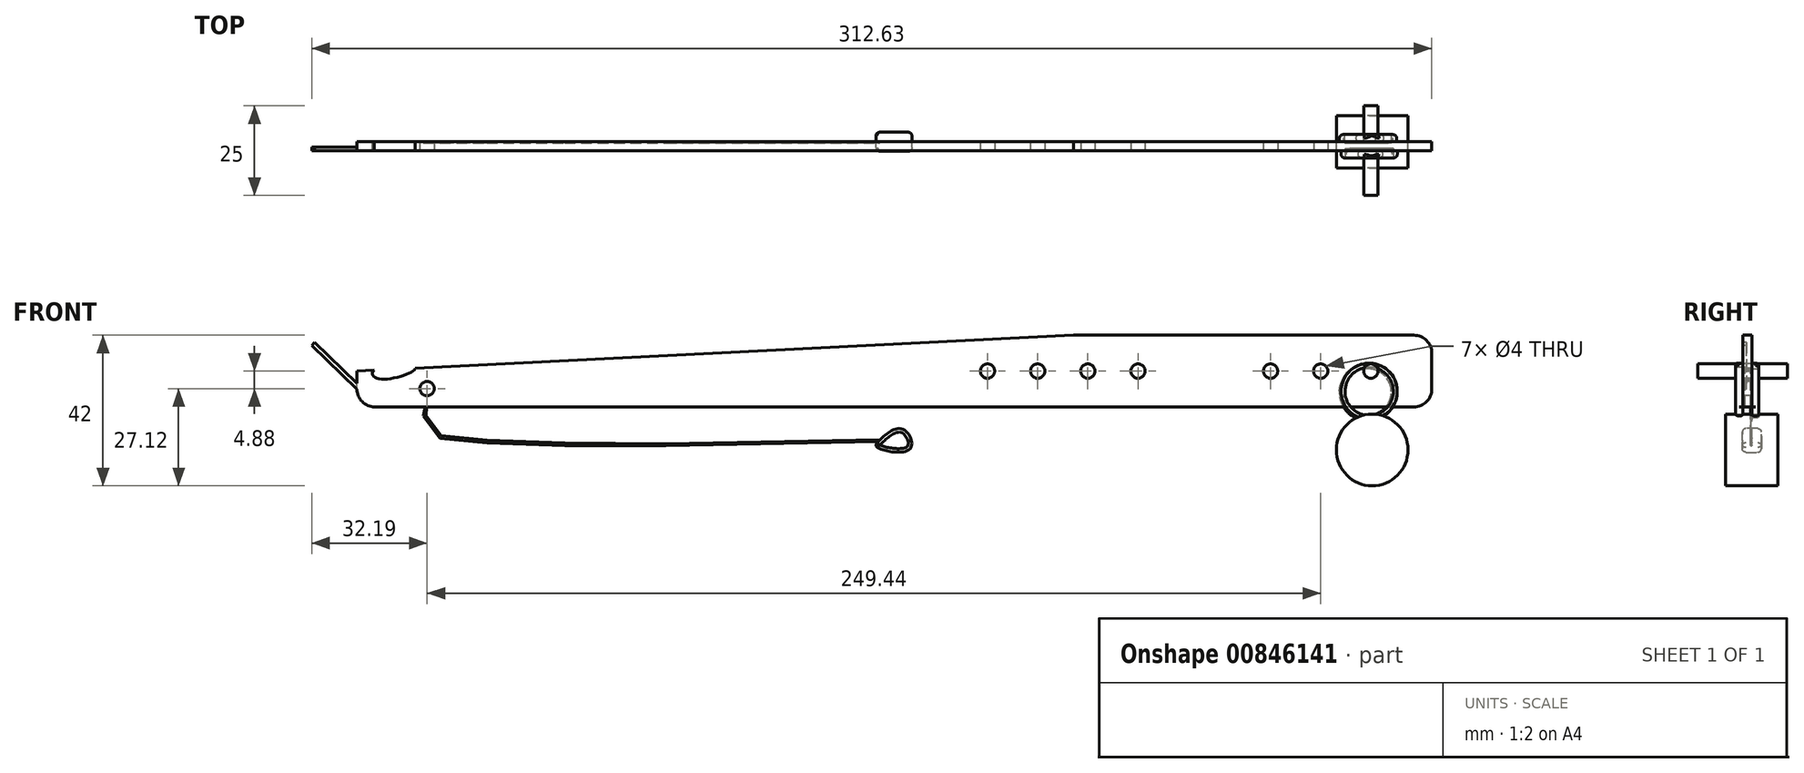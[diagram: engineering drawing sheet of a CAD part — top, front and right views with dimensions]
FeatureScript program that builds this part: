
annotation { "Feature Type Name" : "Feature", "Feature Type Description" : "" }
export const myFeature = defineFeature(function(context is Context, id is Id, definition is map)
    precondition{}
    {
        {
            var Q0;
            Q0=qCreatedBy(makeId("Front.planeOp"),FACE);
            var sketch = newSketch(context, id + "F0", { "sketchPlane" : qUnion([Q0])});
            skLineSegment(sketch, "E0.bottom", {"start": v(150, -10) * mm, "end": v(-150, -10) * mm});
            skLineSegment(sketch, "E0.top", {"start": v(150, 10) * mm, "end": v(-150, 10) * mm});
            skLineSegment(sketch, "E0.left", {"start": v(150, -10) * mm, "end": v(150, 10) * mm});
            skLineSegment(sketch, "E0.right", {"start": v(-150, -10) * mm, "end": v(-150, 10) * mm});
            skPoint(sketch, "E0.middle", {"position": v(0, 0) * mm});
            skSolve(sketch);
        }
        {
            var Q0;
            Q0 = qSketchRegion(id + "F0", true);
            extrude(context, id + "F1", {"entities" : qUnion([Q0]), "depth" : 2.5 * mm, "offsetDistance" : 25 * mm});
        }
        {
            var Q0;
            Q0=makeQuery(id+"F1.opExtrude","SWEPT_EDGE",EDGE,{"disambiguationData":[OSD([sQuery(id+"F0.wireOp",EDGE,"E0.top"),sQuery(id+"F0.wireOp",EDGE,"E0.right")])]});
            chamfer(context, id + "F2", {"entities" : qUnion([Q0]), "chamferType" : ChamferType.TWO_OFFSETS, "width1" : 10 * mm, "oppositeDirection" : false, "width2" : 200 * mm, "tangentPropagation" : true});
        }
        {
            var Q0;
            Q0=makeQuery(id+"F1.opExtrude","SWEPT_EDGE",EDGE,{"disambiguationData":[OSD([sQuery(id+"F0.wireOp",EDGE,"E0.bottom"),sQuery(id+"F0.wireOp",EDGE,"E0.right")])]});
            fillet(context, id + "F3", {"entities" : qUnion([Q0]), "radius" : 5 * mm, "tangentPropagation" : true, "allowEdgeOverflow" : false});
        }
        {
            var Q0;
            Q0=makeQuery(id+"F1.opExtrude","SWEPT_EDGE",EDGE,{"disambiguationData":[OSD([sQuery(id+"F0.wireOp",EDGE,"E0.top"),sQuery(id+"F0.wireOp",EDGE,"E0.left")])]});
            fillet(context, id + "F4", {"entities" : qUnion([Q0]), "radius" : 5 * mm, "tangentPropagation" : true, "allowEdgeOverflow" : false});
        }
        {
            var Q0;
            Q0=makeQuery(id+"F1.opExtrude","SWEPT_EDGE",EDGE,{"disambiguationData":[OSD([sQuery(id+"F0.wireOp",EDGE,"E0.bottom"),sQuery(id+"F0.wireOp",EDGE,"E0.left")])]});
            fillet(context, id + "F5", {"entities" : qUnion([Q0]), "radius" : 5 * mm, "tangentPropagation" : true, "allowEdgeOverflow" : false});
        }
        {
            var Q0;
            Q0=makeQuery(id+"F1.opExtrude","CAP_FACE",FACE,{"disambiguationData":[OSD([sQuery(id+"F0.wireOp",EDGE,"E0.bottom"),sQuery(id+"F0.wireOp",EDGE,"E0.top"),sQuery(id+"F0.wireOp",EDGE,"E0.left"),sQuery(id+"F0.wireOp",EDGE,"E0.right")])],"isStart":false});
            var sketch = newSketch(context, id + "F6", { "sketchPlane" : qUnion([Q0])});
            skFitSpline(sketch, "E1", {"points": [v(-145.2, 0.24) * mm, v(-144.14, -2.13) * mm, v(-133.8, 0.8) * mm, v(-145.2, 0.24) * mm]});
            skSolve(sketch);
        }
        {
            var Q0;
            Q0 = qSketchRegion(id + "F6", true);
            extrude(context, id + "F7", {"entities" : qUnion([Q0]), "operationType" : NewBodyOperationType.REMOVE, "oppositeDirection" : true, "depth" : 6 * mm, "offsetDistance" : 25 * mm});
        }
        {
            var Q0;
            Q0=makeQuery(id+"F1.opExtrude","CAP_FACE",FACE,{"disambiguationData":[OSD([sQuery(id+"F0.wireOp",EDGE,"E0.bottom"),sQuery(id+"F0.wireOp",EDGE,"E0.top"),sQuery(id+"F0.wireOp",EDGE,"E0.left"),sQuery(id+"F0.wireOp",EDGE,"E0.right")])],"isStart":false});
            var sketch = newSketch(context, id + "F8", { "sketchPlane" : qUnion([Q0])});
            skLineSegment(sketch, "E2", {"start": v(-150, -5) * mm, "end": v(-162.63, 7.1) * mm});
            skLineSegment(sketch, "E3", {"start": v(-162.63, 7.1) * mm, "end": v(-161.82, 7.96) * mm});
            skLineSegment(sketch, "E4", {"start": v(-161.82, 7.96) * mm, "end": v(-150, -3.37) * mm});
            skLineSegment(sketch, "E5", {"start": v(-150, -3.37) * mm, "end": v(-150, -5) * mm});
            skSolve(sketch);
        }
        {
            var Q0;
            Q0 = qSketchRegion(id + "F8", true);
            extrude(context, id + "F9", {"entities" : qUnion([Q0]), "operationType" : NewBodyOperationType.ADD, "oppositeDirection" : true, "depth" : 1 * mm, "offsetDistance" : 25 * mm});
        }
        {
            var Q0;
            Q0=makeQuery(id+"F9.boolean.opBoolean","MERGE",FACE,{"derivedFrom":[makeQuery(id+"F1.opExtrude","CAP_FACE",FACE,{"disambiguationData":[OSD([sQuery(id+"F0.wireOp",EDGE,"E0.bottom"),sQuery(id+"F0.wireOp",EDGE,"E0.top"),sQuery(id+"F0.wireOp",EDGE,"E0.left"),sQuery(id+"F0.wireOp",EDGE,"E0.right")])],"isStart":false}),makeQuery(id+"F9.opExtrude","CAP_FACE",FACE,{"disambiguationData":[OSD([sQuery(id+"F8.wireOp",EDGE,"E2"),sQuery(id+"F8.wireOp",EDGE,"E3"),sQuery(id+"F8.wireOp",EDGE,"E4"),sQuery(id+"F8.wireOp",EDGE,"E5")])],"isStart":true})]});
            var sketch = newSketch(context, id + "F10", { "sketchPlane" : qUnion([Q0])});
            skCircle(sketch, "E6", {"center": v(-130.44, -4.88) * mm, "radius": 2 * mm});
            skSolve(sketch);
        }
        {
            var Q0;
            Q0 = qSketchRegion(id + "F10", true);
            extrude(context, id + "F11", {"entities" : qUnion([Q0]), "operationType" : NewBodyOperationType.REMOVE, "oppositeDirection" : true, "depth" : 25 * mm, "offsetDistance" : 25 * mm});
        }
        {
            var Q0;
            Q0=makeQuery(id+"F9.boolean.opBoolean","MERGE",FACE,{"derivedFrom":[makeQuery(id+"F1.opExtrude","CAP_FACE",FACE,{"disambiguationData":[OSD([sQuery(id+"F0.wireOp",EDGE,"E0.bottom"),sQuery(id+"F0.wireOp",EDGE,"E0.top"),sQuery(id+"F0.wireOp",EDGE,"E0.left"),sQuery(id+"F0.wireOp",EDGE,"E0.right")])],"isStart":false}),makeQuery(id+"F9.opExtrude","CAP_FACE",FACE,{"disambiguationData":[OSD([sQuery(id+"F8.wireOp",EDGE,"E2"),sQuery(id+"F8.wireOp",EDGE,"E3"),sQuery(id+"F8.wireOp",EDGE,"E4"),sQuery(id+"F8.wireOp",EDGE,"E5")])],"isStart":true})]});
            var sketch = newSketch(context, id + "F12", { "sketchPlane" : qUnion([Q0])});
            skCircle(sketch, "E7", {"center": v(133, 0) * mm, "radius": 2 * mm});
            skSolve(sketch);
        }
        {
            var Q0;
            Q0 = qSketchRegion(id + "F12", true);
            extrude(context, id + "F13", {"entities" : qUnion([Q0]), "operationType" : NewBodyOperationType.ADD, "endBound" : BoundingType.SYMMETRIC, "oppositeDirection" : true, "depth" : 25 * mm, "offsetDistance" : 25 * mm});
        }
        {
            var Q0;
            Q0=makeQuery(id+"F9.boolean.opBoolean","MERGE",FACE,{"derivedFrom":[makeQuery(id+"F1.opExtrude","CAP_FACE",FACE,{"disambiguationData":[OSD([sQuery(id+"F0.wireOp",EDGE,"E0.bottom"),sQuery(id+"F0.wireOp",EDGE,"E0.top"),sQuery(id+"F0.wireOp",EDGE,"E0.left"),sQuery(id+"F0.wireOp",EDGE,"E0.right")])],"isStart":false}),makeQuery(id+"F9.opExtrude","CAP_FACE",FACE,{"disambiguationData":[OSD([sQuery(id+"F8.wireOp",EDGE,"E2"),sQuery(id+"F8.wireOp",EDGE,"E3"),sQuery(id+"F8.wireOp",EDGE,"E4"),sQuery(id+"F8.wireOp",EDGE,"E5")])],"isStart":true})]});
            var sketch = newSketch(context, id + "F14", { "sketchPlane" : qUnion([Q0])});
            skCircle(sketch, "E8", {"center": v(119, 0) * mm, "radius": 2 * mm});
            skSolve(sketch);
        }
        {
            var Q0;
            Q0=makeQuery(id+"F14.imprint","IMPRINT",FACE,{"disambiguationData":[TD([[makeQuery(id+"F14.imprint","IMPRINT",EDGE,{"derivedFrom":sQuery(id+"F14.wireOp",EDGE,"E8")}),-1.0]])]});
            var sketch = newSketch(context, id + "F15", { "sketchPlane" : qUnion([Q0])});
            skCircle(sketch, "E9", {"center": v(105, 0) * mm, "radius": 2 * mm});
            skSolve(sketch);
        }
        {
            var Q0;
            Q0 = qSketchRegion(id + "F14", true);
            extrude(context, id + "F16", {"entities" : qUnion([Q0]), "operationType" : NewBodyOperationType.REMOVE, "oppositeDirection" : true, "depth" : 25 * mm, "offsetDistance" : 25 * mm});
        }
        {
            var Q0;
            Q0 = qSketchRegion(id + "F15", true);
            extrude(context, id + "F17", {"entities" : qUnion([Q0]), "operationType" : NewBodyOperationType.REMOVE, "oppositeDirection" : true, "depth" : 25 * mm, "offsetDistance" : 25 * mm});
        }
        {
            var Q0;
            Q0=makeQuery(id+"F9.boolean.opBoolean","MERGE",FACE,{"derivedFrom":[makeQuery(id+"F1.opExtrude","CAP_FACE",FACE,{"disambiguationData":[OSD([sQuery(id+"F0.wireOp",EDGE,"E0.bottom"),sQuery(id+"F0.wireOp",EDGE,"E0.top"),sQuery(id+"F0.wireOp",EDGE,"E0.left"),sQuery(id+"F0.wireOp",EDGE,"E0.right")])],"isStart":false}),makeQuery(id+"F9.opExtrude","CAP_FACE",FACE,{"disambiguationData":[OSD([sQuery(id+"F8.wireOp",EDGE,"E2"),sQuery(id+"F8.wireOp",EDGE,"E3"),sQuery(id+"F8.wireOp",EDGE,"E4"),sQuery(id+"F8.wireOp",EDGE,"E5")])],"isStart":true})]});
            var sketch = newSketch(context, id + "F18", { "sketchPlane" : qUnion([Q0])});
            skCircle(sketch, "E10", {"center": v(68, 0) * mm, "radius": 2 * mm});
            skSolve(sketch);
        }
        {
            var Q0;
            Q0 = qSketchRegion(id + "F18", true);
            extrude(context, id + "F19", {"entities" : qUnion([Q0]), "operationType" : NewBodyOperationType.REMOVE, "oppositeDirection" : true, "depth" : 25 * mm, "offsetDistance" : 25 * mm});
        }
        {
            var Q0;
            Q0=makeQuery(id+"F9.boolean.opBoolean","MERGE",FACE,{"derivedFrom":[makeQuery(id+"F1.opExtrude","CAP_FACE",FACE,{"disambiguationData":[OSD([sQuery(id+"F0.wireOp",EDGE,"E0.bottom"),sQuery(id+"F0.wireOp",EDGE,"E0.top"),sQuery(id+"F0.wireOp",EDGE,"E0.left"),sQuery(id+"F0.wireOp",EDGE,"E0.right")])],"isStart":false}),makeQuery(id+"F9.opExtrude","CAP_FACE",FACE,{"disambiguationData":[OSD([sQuery(id+"F8.wireOp",EDGE,"E2"),sQuery(id+"F8.wireOp",EDGE,"E3"),sQuery(id+"F8.wireOp",EDGE,"E4"),sQuery(id+"F8.wireOp",EDGE,"E5")])],"isStart":true})]});
            var sketch = newSketch(context, id + "F20", { "sketchPlane" : qUnion([Q0])});
            skCircle(sketch, "E11", {"center": v(54, 0) * mm, "radius": 2 * mm});
            skSolve(sketch);
        }
        {
            var Q0;
            Q0 = qSketchRegion(id + "F20", true);
            extrude(context, id + "F21", {"entities" : qUnion([Q0]), "operationType" : NewBodyOperationType.REMOVE, "oppositeDirection" : true, "depth" : 25 * mm, "offsetDistance" : 25 * mm});
        }
        {
            var Q0;
            Q0=makeQuery(id+"F9.boolean.opBoolean","MERGE",FACE,{"derivedFrom":[makeQuery(id+"F1.opExtrude","CAP_FACE",FACE,{"disambiguationData":[OSD([sQuery(id+"F0.wireOp",EDGE,"E0.bottom"),sQuery(id+"F0.wireOp",EDGE,"E0.top"),sQuery(id+"F0.wireOp",EDGE,"E0.left"),sQuery(id+"F0.wireOp",EDGE,"E0.right")])],"isStart":false}),makeQuery(id+"F9.opExtrude","CAP_FACE",FACE,{"disambiguationData":[OSD([sQuery(id+"F8.wireOp",EDGE,"E2"),sQuery(id+"F8.wireOp",EDGE,"E3"),sQuery(id+"F8.wireOp",EDGE,"E4"),sQuery(id+"F8.wireOp",EDGE,"E5")])],"isStart":true})]});
            var sketch = newSketch(context, id + "F22", { "sketchPlane" : qUnion([Q0])});
            skCircle(sketch, "E12", {"center": v(40, 0) * mm, "radius": 2 * mm});
            skSolve(sketch);
        }
        {
            var Q0;
            Q0 = qSketchRegion(id + "F22", true);
            extrude(context, id + "F23", {"entities" : qUnion([Q0]), "operationType" : NewBodyOperationType.REMOVE, "oppositeDirection" : true, "depth" : 25 * mm, "offsetDistance" : 25 * mm});
        }
        {
            var Q0;
            Q0=makeQuery(id+"F9.boolean.opBoolean","MERGE",FACE,{"derivedFrom":[makeQuery(id+"F1.opExtrude","CAP_FACE",FACE,{"disambiguationData":[OSD([sQuery(id+"F0.wireOp",EDGE,"E0.bottom"),sQuery(id+"F0.wireOp",EDGE,"E0.top"),sQuery(id+"F0.wireOp",EDGE,"E0.left"),sQuery(id+"F0.wireOp",EDGE,"E0.right")])],"isStart":false}),makeQuery(id+"F9.opExtrude","CAP_FACE",FACE,{"disambiguationData":[OSD([sQuery(id+"F8.wireOp",EDGE,"E2"),sQuery(id+"F8.wireOp",EDGE,"E3"),sQuery(id+"F8.wireOp",EDGE,"E4"),sQuery(id+"F8.wireOp",EDGE,"E5")])],"isStart":true})]});
            var sketch = newSketch(context, id + "F24", { "sketchPlane" : qUnion([Q0])});
            skCircle(sketch, "E13", {"center": v(26, 0) * mm, "radius": 2 * mm});
            skSolve(sketch);
        }
        {
            var Q0;
            Q0 = qSketchRegion(id + "F24", true);
            extrude(context, id + "F25", {"entities" : qUnion([Q0]), "operationType" : NewBodyOperationType.REMOVE, "oppositeDirection" : true, "depth" : 25 * mm, "offsetDistance" : 25 * mm});
        }
        {
            var Q0;
            Q0=makeQuery(id+"F9.boolean.opBoolean","MERGE",FACE,{"derivedFrom":[makeQuery(id+"F1.opExtrude","CAP_FACE",FACE,{"disambiguationData":[OSD([sQuery(id+"F0.wireOp",EDGE,"E0.bottom"),sQuery(id+"F0.wireOp",EDGE,"E0.top"),sQuery(id+"F0.wireOp",EDGE,"E0.left"),sQuery(id+"F0.wireOp",EDGE,"E0.right")])],"isStart":false}),makeQuery(id+"F9.opExtrude","CAP_FACE",FACE,{"disambiguationData":[OSD([sQuery(id+"F8.wireOp",EDGE,"E2"),sQuery(id+"F8.wireOp",EDGE,"E3"),sQuery(id+"F8.wireOp",EDGE,"E4"),sQuery(id+"F8.wireOp",EDGE,"E5")])],"isStart":true})]});
            var sketch = newSketch(context, id + "F26", { "sketchPlane" : qUnion([Q0])});
            skCircle(sketch, "E14", {"center": v(132.53, -5.65) * mm, "radius": 7.84 * mm});
            skSolve(sketch);
        }
        {
            var Q0;
            Q0 = qSketchRegion(id + "F26", true);
            extrude(context, id + "F27", {"entities" : qUnion([Q0]), "operationType" : NewBodyOperationType.ADD, "depth" : 2 * mm, "offsetDistance" : 25 * mm});
        }
        {
            var Q0;
            Q0=makeQuery(id+"F27.opExtrude","CAP_FACE",FACE,{"disambiguationData":[OSD([sQuery(id+"F26.wireOp",EDGE,"E14")])],"isStart":false});
            var sketch = newSketch(context, id + "F28", { "sketchPlane" : qUnion([Q0])});
            skCircle(sketch, "E15", {"center": v(132.53, -5.65) * mm, "radius": 6.74 * mm});
            skSolve(sketch);
        }
        {
            var Q0;
            Q0 = qSketchRegion(id + "F28", true);
            extrude(context, id + "F29", {"entities" : qUnion([Q0]), "operationType" : NewBodyOperationType.REMOVE, "oppositeDirection" : true, "depth" : 2.6 * mm, "offsetDistance" : 25 * mm});
        }
        {
            var Q0;
            Q0=makeQuery(id+"F1.opExtrude","CAP_FACE",FACE,{"disambiguationData":[OSD([sQuery(id+"F0.wireOp",EDGE,"E0.bottom"),sQuery(id+"F0.wireOp",EDGE,"E0.top"),sQuery(id+"F0.wireOp",EDGE,"E0.left"),sQuery(id+"F0.wireOp",EDGE,"E0.right")])],"isStart":true});
            var sketch = newSketch(context, id + "F30", { "sketchPlane" : qUnion([Q0])});
            skCircle(sketch, "E16", {"center": v(-132.22, -5.88) * mm, "radius": 8 * mm});
            skSolve(sketch);
        }
        {
            var Q0;
            Q0 = qSketchRegion(id + "F30", true);
            extrude(context, id + "F31", {"entities" : qUnion([Q0]), "operationType" : NewBodyOperationType.ADD, "depth" : 2 * mm, "offsetDistance" : 25 * mm});
        }
        {
            var Q0;
            Q0=makeQuery(id+"F31.opExtrude","CAP_FACE",FACE,{"disambiguationData":[OSD([sQuery(id+"F30.wireOp",EDGE,"E16")])],"isStart":false});
            var sketch = newSketch(context, id + "F32", { "sketchPlane" : qUnion([Q0])});
            skCircle(sketch, "E17", {"center": v(-132.22, -5.88) * mm, "radius": 6.5 * mm});
            skSolve(sketch);
        }
        {
            var Q0;
            Q0 = qSketchRegion(id + "F32", true);
            extrude(context, id + "F33", {"entities" : qUnion([Q0]), "operationType" : NewBodyOperationType.REMOVE, "oppositeDirection" : true, "depth" : 2.4 * mm, "offsetDistance" : 25 * mm});
        }
        {
            var Q0;
            Q0=makeQuery(id+"F31.opExtrude","CAP_EDGE",EDGE,{"disambiguationData":[OSD([sQuery(id+"F30.wireOp",EDGE,"E16")])],"isStart":false});
            fillet(context, id + "F34", {"entities" : qUnion([Q0]), "radius" : 1 * mm, "tangentPropagation" : true, "allowEdgeOverflow" : false});
        }
        {
            var Q0;
            Q0=makeQuery(id+"F27.opExtrude","CAP_EDGE",EDGE,{"disambiguationData":[OSD([sQuery(id+"F26.wireOp",EDGE,"E14")])],"isStart":false});
            fillet(context, id + "F35", {"entities" : qUnion([Q0]), "radius" : 1 * mm, "tangentPropagation" : true, "allowEdgeOverflow" : false});
        }
        {
            var Q0;
            {var subQ0=sQuery(id+"F26.wireOp",EDGE,"E14");Q0=makeQuery(id+"F27.boolean.opBoolean","SPLIT",EDGE,{"disambiguationData":[topologyDisambiguationEdgeConnected([makeQuery(id+"F27.opExtrude","CAP_FACE",FACE,{"disambiguationData":[OSD([subQ0])],"isStart":true})])],"derivedFrom":makeQuery(id+"F27.opExtrude","CAP_EDGE",EDGE,{"disambiguationData":[OSD([subQ0])],"isStart":true})});}
            fillet(context, id + "F36", {"entities" : qUnion([Q0]), "radius" : 1 * mm, "tangentPropagation" : true, "allowEdgeOverflow" : false});
        }
        {
            var Q0;
            {var subQ0=sQuery(id+"F30.wireOp",EDGE,"E16");Q0=makeQuery(id+"F31.boolean.opBoolean","SPLIT",EDGE,{"disambiguationData":[topologyDisambiguationEdgeConnected([makeQuery(id+"F31.opExtrude","CAP_FACE",FACE,{"disambiguationData":[OSD([subQ0])],"isStart":true})])],"derivedFrom":makeQuery(id+"F31.opExtrude","CAP_EDGE",EDGE,{"disambiguationData":[OSD([subQ0])],"isStart":true})});}
            fillet(context, id + "F37", {"entities" : qUnion([Q0]), "radius" : 1 * mm, "tangentPropagation" : true, "allowEdgeOverflow" : false});
        }
        {
            var Q0;
            Q0=qCreatedBy(makeId("Front.planeOp"),FACE);
            var sketch = newSketch(context, id + "F38", { "sketchPlane" : qUnion([Q0])});
            skLineSegment(sketch, "E18", {"start": v(-130.5, -6.89) * mm, "end": v(-131.46, -12.56) * mm});
            skLineSegment(sketch, "E19", {"start": v(-131.46, -12.56) * mm, "end": v(-126.84, -18.75) * mm});
            skLineSegment(sketch, "E20", {"start": v(-126.84, -18.75) * mm, "end": v(-113.75, -20) * mm});
            skLineSegment(sketch, "E21", {"start": v(-113.75, -20) * mm, "end": v(-92.04, -20.75) * mm});
            skLineSegment(sketch, "E22", {"start": v(-92.04, -20.75) * mm, "end": v(-63.78, -20.75) * mm});
            skLineSegment(sketch, "E23", {"start": v(-63.78, -20.75) * mm, "end": v(-24.45, -20) * mm});
            skLineSegment(sketch, "E24", {"start": v(-24.45, -20) * mm, "end": v(-4.04, -19.62) * mm});
            skLineSegment(sketch, "E25", {"start": v(-4.04, -19.62) * mm, "end": v(-4.05, -19.14) * mm});
            skLineSegment(sketch, "E26", {"start": v(-4.05, -19.14) * mm, "end": v(-63.78, -20.27) * mm});
            skLineSegment(sketch, "E27", {"start": v(-63.78, -20.27) * mm, "end": v(-92.04, -20) * mm});
            skLineSegment(sketch, "E28", {"start": v(-92.04, -20) * mm, "end": v(-113.75, -19.26) * mm});
            skLineSegment(sketch, "E29", {"start": v(-113.75, -19.26) * mm, "end": v(-126.5, -18.04) * mm});
            skLineSegment(sketch, "E30", {"start": v(-126.5, -18.04) * mm, "end": v(-130.69, -12.43) * mm});
            skLineSegment(sketch, "E31", {"start": v(-130.69, -12.43) * mm, "end": v(-130.5, -6.89) * mm});
            skSolve(sketch);
        }
        {
            var Q0;
            Q0 = qSketchRegion(id + "F38", true);
            extrude(context, id + "F39", {"entities" : qUnion([Q0]), "operationType" : NewBodyOperationType.ADD, "depth" : 0.4 * mm, "offsetDistance" : 25 * mm});
        }
        {
            var Q0;
            Q0=makeQuery(id+"F39.opExtrude","CAP_EDGE",EDGE,{"disambiguationData":[OSD([sQuery(id+"F38.wireOp",EDGE,"E30")])],"isStart":true});
            var Q1;
            Q1=makeQuery(id+"F39.opExtrude","CAP_EDGE",EDGE,{"disambiguationData":[OSD([sQuery(id+"F38.wireOp",EDGE,"E29")])],"isStart":true});
            var Q2;
            Q2=makeQuery(id+"F39.opExtrude","CAP_EDGE",EDGE,{"disambiguationData":[OSD([sQuery(id+"F38.wireOp",EDGE,"E28")])],"isStart":true});
            var Q3;
            Q3=makeQuery(id+"F39.opExtrude","CAP_EDGE",EDGE,{"disambiguationData":[OSD([sQuery(id+"F38.wireOp",EDGE,"E27")])],"isStart":true});
            var Q4;
            Q4=makeQuery(id+"F39.opExtrude","CAP_EDGE",EDGE,{"disambiguationData":[OSD([sQuery(id+"F38.wireOp",EDGE,"E26")])],"isStart":true});
            fillet(context, id + "F40", {"entities" : qUnion([Q0, Q1, Q2, Q3, Q4]), "radius" : 1 * mm, "tangentPropagation" : true, "allowEdgeOverflow" : false});
        }
        {
            var Q0;
            Q0=qCreatedBy(makeId("Front.planeOp"),FACE);
            var sketch = newSketch(context, id + "F41", { "sketchPlane" : qUnion([Q0])});
            skFitSpline(sketch, "E32", {"points": [v(-4.2, -19.34) * mm, v(2.22, -16.19) * mm, v(4.36, -21.73) * mm, v(-4.9, -21.16) * mm, v(-4.2, -19.34) * mm]});
            skSolve(sketch);
        }
        {
            var Q0;
            Q0 = qSketchRegion(id + "F41", true);
            extrude(context, id + "F42", {"entities" : qUnion([Q0]), "operationType" : NewBodyOperationType.ADD, "endBound" : BoundingType.SYMMETRIC, "depth" : 5.3 * mm, "offsetDistance" : 25 * mm});
        }
        {
            var Q0;
            Q0=makeQuery(id+"F42.opExtrude","CAP_EDGE",EDGE,{"disambiguationData":[OSD([sQuery(id+"F41.wireOp",EDGE,"E32")])],"isStart":true});
            var Q1;
            Q1=makeQuery(id+"F42.opExtrude","CAP_EDGE",EDGE,{"disambiguationData":[OSD([sQuery(id+"F41.wireOp",EDGE,"E32")])],"isStart":false});
            fillet(context, id + "F43", {"entities" : qUnion([Q0, Q1]), "radius" : 1 * mm, "tangentPropagation" : true, "allowEdgeOverflow" : false});
        }
        {
            var Q0;
            Q0=qCreatedBy(makeId("Front.planeOp"),FACE);
            var sketch = newSketch(context, id + "F44", { "sketchPlane" : qUnion([Q0])});
            skCircle(sketch, "E33", {"center": v(133.36, -22) * mm, "radius": 10 * mm});
            skSolve(sketch);
        }
        {
            var Q0;
            Q0 = qSketchRegion(id + "F44", true);
            extrude(context, id + "F45", {"entities" : qUnion([Q0]), "operationType" : NewBodyOperationType.ADD, "endBound" : BoundingType.SYMMETRIC, "depth" : 14.6 * mm, "offsetDistance" : 25 * mm});
        }
    });
